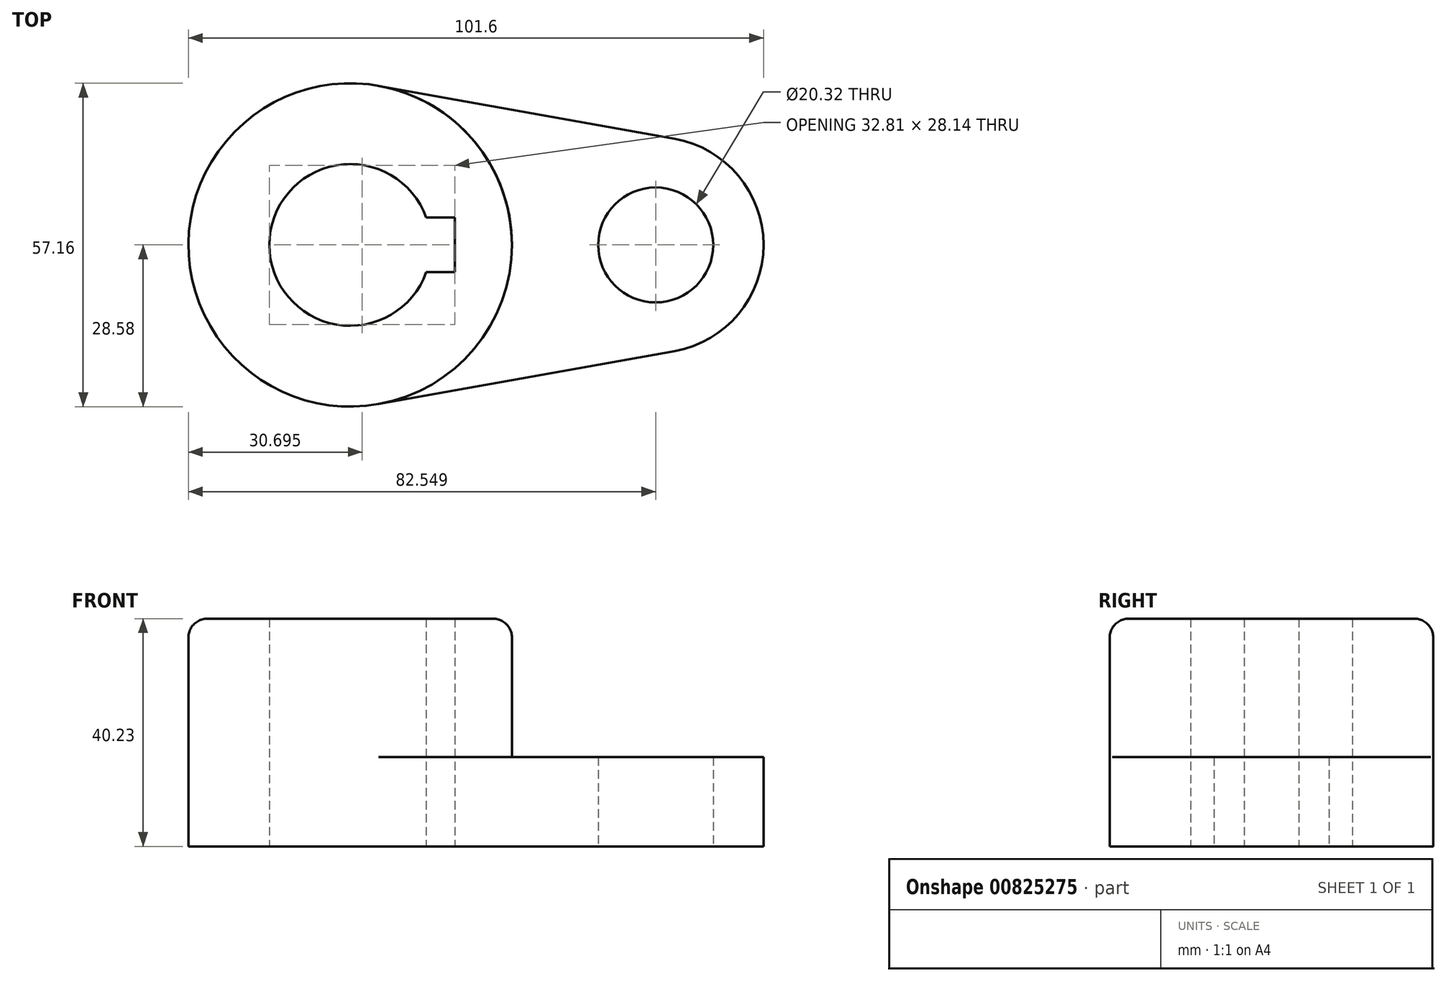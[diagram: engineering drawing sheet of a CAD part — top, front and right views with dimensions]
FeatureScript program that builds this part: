
annotation { "Feature Type Name" : "Feature", "Feature Type Description" : "" }
export const myFeature = defineFeature(function(context is Context, id is Id, definition is map)
    precondition{}
    {
        {
            var Q0;
            Q0=qCreatedBy(makeId("Top.planeOp"),FACE);
            var sketch = newSketch(context, id + "F0", { "sketchPlane" : qUnion([Q0])});
            skCircle(sketch, "E0", {"center": v(-30.62, 0) * mm, "radius": 28.58 * mm});
            skCircle(sketch, "E1", {"center": v(23.36, 0) * mm, "radius": 10.16 * mm});
            skLineSegment(sketch, "E2", {"start": v(-17.17, 4.83) * mm, "end": v(-12.1, 4.83) * mm});
            skLineSegment(sketch, "E3", {"start": v(-17.17, -4.83) * mm, "end": v(-12.1, -4.83) * mm});
            skLineSegment(sketch, "E4", {"start": v(-12.1, -4.83) * mm, "end": v(-12.1, 4.83) * mm});
            skLineSegment(sketch, "E5", {"start": v(-25.57, 28.13) * mm, "end": v(26.72, 18.75) * mm});
            skLineSegment(sketch, "E6", {"start": v(-25.57, -28.13) * mm, "end": v(26.72, -18.75) * mm});
            skArc(sketch, "E7", {"start": v(26.72, -18.75) * mm, "mid": v(42.4, 0) * mm, "end": v(26.72, 18.75) * mm});
            skArc(sketch, "E8", {"start": v(-17.17, 4.83) * mm, "mid": v(-44.9, 0) * mm, "end": v(-17.17, -4.83) * mm});
            skSolve(sketch);
        }
        {
            var Q0;
            Q0=makeQuery(id+"F0.imprint","IMPRINT",FACE,{"disambiguationData":[TD([[makeQuery(id+"F0.imprint","IMPRINT",EDGE,{"derivedFrom":sQuery(id+"F0.wireOp",EDGE,"E2")}),1.0]])]});
            extrude(context, id + "F1", {"entities" : qUnion([Q0]), "depth" : 40.23 * mm, "offsetDistance" : 25.4 * mm});
        }
        {
            var Q0;
            Q0=makeQuery(id+"F0.imprint","IMPRINT",FACE,{"disambiguationData":[TD([[makeQuery(id+"F0.imprint","IMPRINT",EDGE,{"derivedFrom":sQuery(id+"F0.wireOp",EDGE,"E1")}),-1.0]])]});
            extrude(context, id + "F2", {"entities" : qUnion([Q0]), "operationType" : NewBodyOperationType.ADD, "depth" : 15.77 * mm, "offsetDistance" : 25.4 * mm});
        }
        {
            var Q0;
            Q0=makeQuery(id+"F1.opExtrude","CAP_EDGE",EDGE,{"disambiguationData":[OSD([sQuery(id+"F0.wireOp",EDGE,"E0")])],"isStart":false});
            fillet(context, id + "F3", {"entities" : qUnion([Q0]), "radius" : 3.3 * mm, "tangentPropagation" : true, "allowEdgeOverflow" : false});
        }
    });
